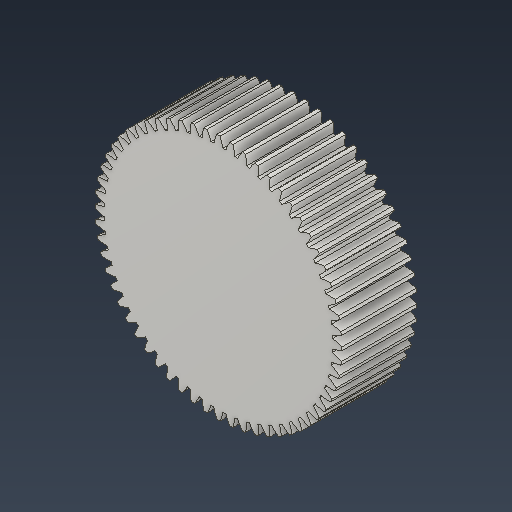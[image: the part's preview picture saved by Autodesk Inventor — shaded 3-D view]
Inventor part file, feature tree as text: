
AUTODESK INVENTOR PART (.ipt)
format: ipt  version: 2021 (Build 250183000, 183)  size: 402,944 bytes
history: native  units: mm (DEFAULTED — no unit token found)
features: plane x3, other x3, sketch x2, extrude x1
ambient origin geometry x8: Origin, YZ Plane, XZ Plane, XY Plane, X Axis, Y Axis, Z Axis, Center Point
bodies: Solid1 (feature_tree)
feature tree (9):
  extrude  "Extrusion1"  Depth=1.7mm TaperAngle=0.0deg
  plane  "Work Plane2"
  plane  "Work Plane8"
  plane  "Work Plane9"
  other  "Engrenagem reta"
  sketch  "Sketch1"  dims[d0=5.575177mm d1=1.7mm d2=0.0mm]
  sketch  "Sketch2"  dims[d3=5.4mm d4=10.0mm d5=0.0mm d16=3.597588mm d17=0.0mm d34=0.523599mm d39=0.0mm d41=0.0mm d43=3.597588mm d46=3.597588mm d47=0.0mm d48=0.0mm]
  other  "Srf1"
  other  "Diâmetro do flanco"
